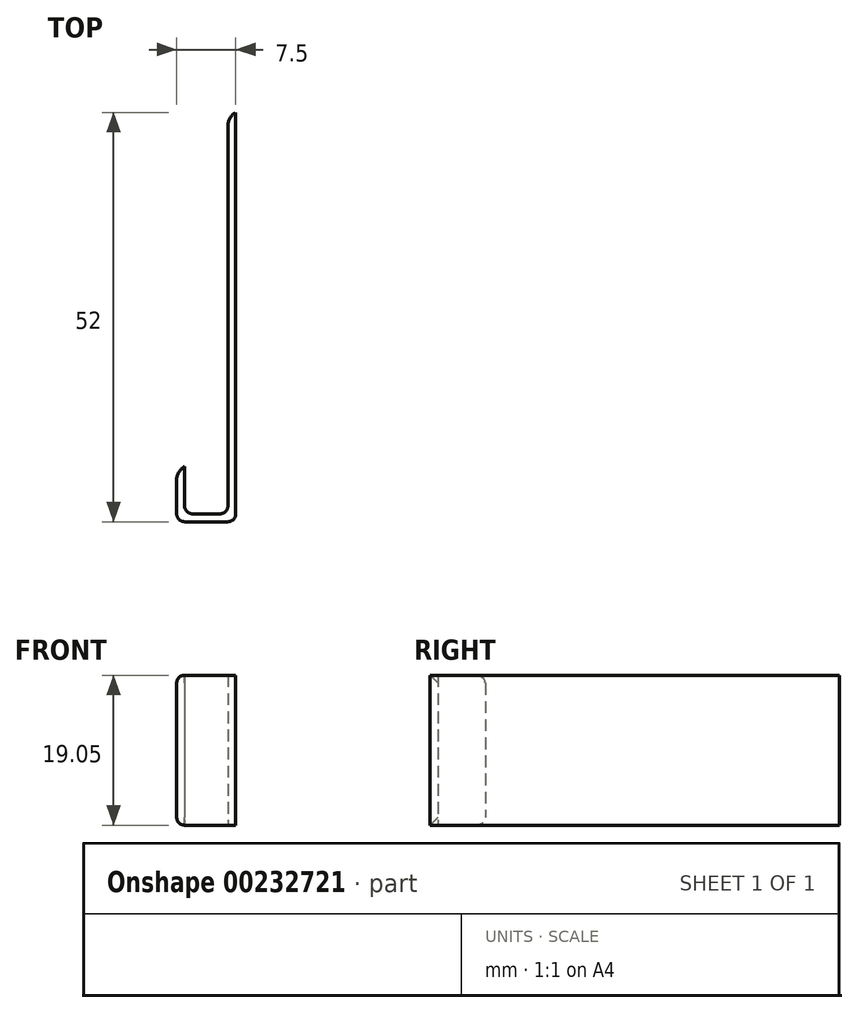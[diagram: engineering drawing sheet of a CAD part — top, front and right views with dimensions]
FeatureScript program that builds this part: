
annotation { "Feature Type Name" : "Feature", "Feature Type Description" : "" }
export const myFeature = defineFeature(function(context is Context, id is Id, definition is map)
    precondition{}
    {
        {
            assignVariable(context, id + "F0", {"variableType" : VariableType.LENGTH, "name" : "holderWidth", "lengthValue" : 19.05 * mm});
        }
        {
            var Q0;
            Q0=qCreatedBy(makeId("Top.planeOp"),FACE);
            var sketch = newSketch(context, id + "F1", { "sketchPlane" : qUnion([Q0])});
            skLineSegment(sketch, "E0", {"start": v(0, 0) * mm, "end": v(0, 52) * mm});
            skLineSegment(sketch, "E1", {"start": v(0, 0) * mm, "end": v(-7.5, 0) * mm});
            skLineSegment(sketch, "E2", {"start": v(-7.5, 0) * mm, "end": v(-7.5, 7) * mm});
            skLineSegment(sketch, "E3", {"start": v(-7.5, 7) * mm, "end": v(-6.5, 7) * mm});
            skLineSegment(sketch, "E4", {"start": v(-6.5, 7) * mm, "end": v(-6.5, 1) * mm});
            skLineSegment(sketch, "E5", {"start": v(-6.5, 1) * mm, "end": v(-1, 1) * mm});
            skLineSegment(sketch, "E6", {"start": v(-1, 1) * mm, "end": v(-1, 52) * mm});
            skLineSegment(sketch, "E7", {"start": v(-1, 52) * mm, "end": v(0, 52) * mm});
            skSolve(sketch);
        }
        {
            var Q0;
            Q0 = qSketchRegion(id + "F1", true);
            extrude(context, id + "F2", {"entities" : qUnion([Q0]), "flatOperationType" : FlatOperationType.REMOVE, "offsetDistance" : 25 * mm, "depth" : getVariable(context, 'holderWidth'), "domain" : OperationDomain.MODEL});
        }
        {
            var Q0;
            Q0=makeQuery(id+"F2.opExtrude","SWEPT_EDGE",EDGE,{"disambiguationData":[OSD([sQuery(id+"F1.wireOp",EDGE,"E2"),sQuery(id+"F1.wireOp",EDGE,"E3")])]});
            var Q1;
            Q1=makeQuery(id+"F2.opExtrude","SWEPT_EDGE",EDGE,{"disambiguationData":[OSD([sQuery(id+"F1.wireOp",EDGE,"E6"),sQuery(id+"F1.wireOp",EDGE,"E7")])]});
            fillet(context, id + "F3", {"entities" : qUnion([Q0, Q1]), "radius" : 2 * mm, "tangentPropagation" : true, "allowEdgeOverflow" : false});
        }
        {
            var Q0;
            Q0=makeQuery(id+"F2.opExtrude","CAP_EDGE",EDGE,{"disambiguationData":[OSD([sQuery(id+"F1.wireOp",EDGE,"E2")])],"isStart":false});
            var Q1;
            Q1=makeQuery(id+"F2.opExtrude","CAP_EDGE",EDGE,{"disambiguationData":[OSD([sQuery(id+"F1.wireOp",EDGE,"E2")])],"isStart":true});
            var Q2;
            Q2=makeQuery(id+"F2.opExtrude","SWEPT_EDGE",EDGE,{"disambiguationData":[OSD([sQuery(id+"F1.wireOp",EDGE,"E1"),sQuery(id+"F1.wireOp",EDGE,"E2")])]});
            var Q3;
            Q3=makeQuery(id+"F2.opExtrude","SWEPT_EDGE",EDGE,{"disambiguationData":[OSD([sQuery(id+"F1.wireOp",EDGE,"E0"),sQuery(id+"F1.wireOp",EDGE,"E1")])]});
            var Q4;
            Q4=makeQuery(id+"F2.opExtrude","SWEPT_EDGE",EDGE,{"disambiguationData":[OSD([sQuery(id+"F1.wireOp",EDGE,"E4"),sQuery(id+"F1.wireOp",EDGE,"E5")])]});
            var Q5;
            Q5=makeQuery(id+"F2.opExtrude","SWEPT_EDGE",EDGE,{"disambiguationData":[OSD([sQuery(id+"F1.wireOp",EDGE,"E5"),sQuery(id+"F1.wireOp",EDGE,"E6")])]});
            fillet(context, id + "F4", {"entities" : qUnion([Q0, Q1, Q2, Q3, Q4, Q5]), "radius" : 1 * mm, "tangentPropagation" : true, "allowEdgeOverflow" : false});
        }
    });
